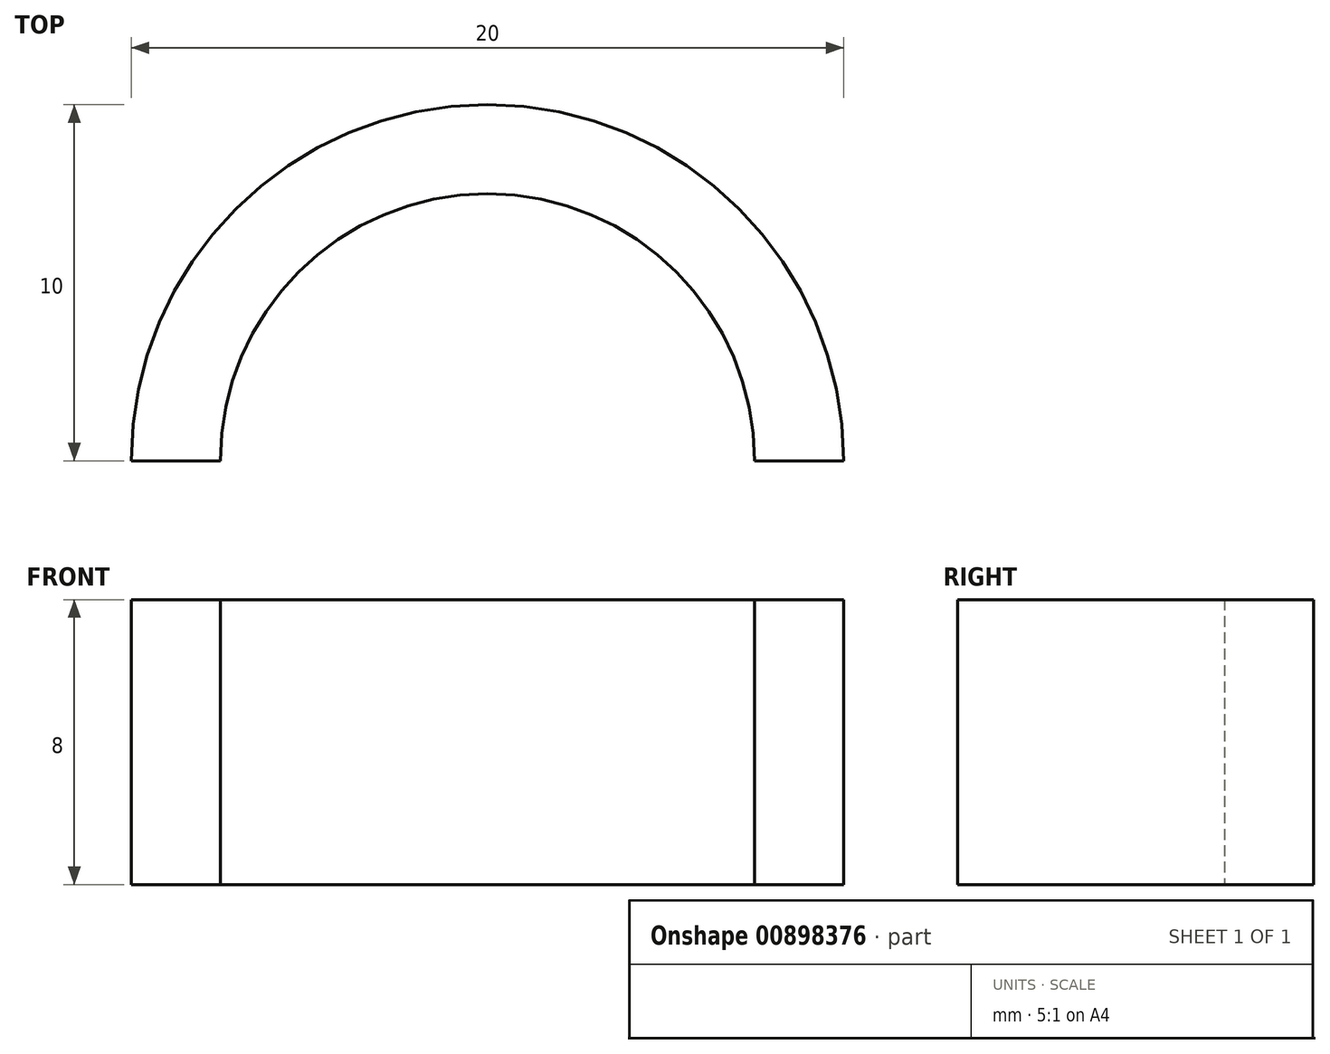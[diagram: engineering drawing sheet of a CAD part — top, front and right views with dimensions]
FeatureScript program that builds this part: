
annotation { "Feature Type Name" : "Feature", "Feature Type Description" : "" }
export const myFeature = defineFeature(function(context is Context, id is Id, definition is map)
    precondition{}
    {
        {
            var Q0;
            Q0=qCreatedBy(makeId("Top.planeOp"),FACE);
            var sketch = newSketch(context, id + "F0", { "sketchPlane" : qUnion([Q0])});
            skLineSegment(sketch, "E0", {"start": v(-10, 0) * mm, "end": v(10, 0) * mm});
            skArc(sketch, "E1", {"start": v(-7.5, 0) * mm, "mid": v(0, 7.5) * mm, "end": v(7.5, 0) * mm});
            skArc(sketch, "E2", {"start": v(-10, 0) * mm, "mid": v(0, 10) * mm, "end": v(10, 0) * mm});
            skArc(sketch, "E3", {"start": v(-2.5, 0) * mm, "mid": v(0, 2.5) * mm, "end": v(2.5, 0) * mm});
            skSolve(sketch);
        }
        {
            assignVariable(context, id + "F1", {"name" : "l", "anyValue" : 8});
        }
        {
            var Q0;
            {var subQ0=sQuery(id+"F0.wireOp",EDGE,"E1");Q0=makeQuery(id+"F0.imprint","IMPRINT",FACE,{"disambiguationData":[TD([[makeQuery(id+"F0.imprint","IMPRINT",EDGE,{"derivedFrom":subQ0}),-1.0]])]});}
            extrude(context, id + "F2", {"entities" : qUnion([Q0]), "depth" : (getVariable(context, 'l')) * mm, "offsetDistance" : 25 * mm});
        }
        {
            var Q0;
            Q0 = qSketchRegion(id + "F0", true);
            extrude(context, id + "F3", {"entities" : qUnion([Q0]), "operationType" : NewBodyOperationType.ADD, "depth" : getVariable(context, 'l') / 2 * mm, "offsetDistance" : 25 * mm});
        }
        {
            var Q0;
            {var subQ1=sQuery(id+"F0.wireOp",EDGE,"E0");var subQ2=sQuery(id+"F0.wireOp",EDGE,"E3");Q0=makeQuery(id+"F3.boolean.opBoolean","SPLIT",FACE,{"disambiguationData":[TD([makeQuery(id+"F2.opExtrude","SWEPT_FACE",FACE,{"disambiguationData":[OSD([subQ2])]})])],"derivedFrom":makeQuery(id+"F3.opExtrude","CAP_FACE",FACE,{"disambiguationData":[OSD([subQ1,sQuery(id+"F0.wireOp",EDGE,"E2")])],"isStart":false})});}
            extrude(context, id + "F4", {"entities" : qUnion([Q0]), "operationType" : NewBodyOperationType.REMOVE, "oppositeDirection" : true, "depth" : 25 * mm, "offsetDistance" : 25 * mm});
        }
    });
